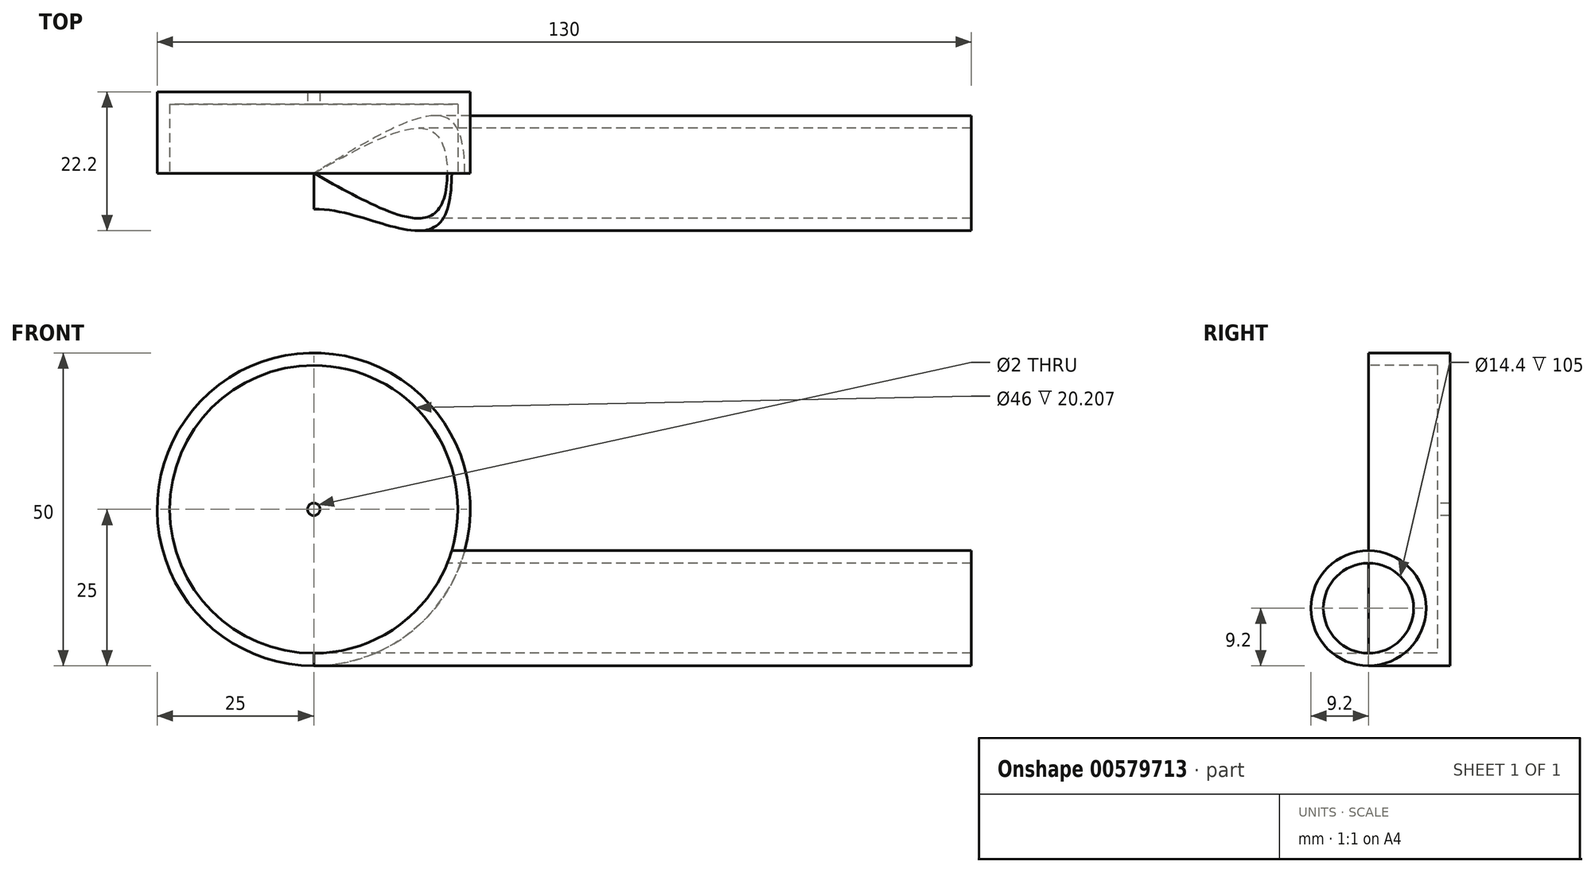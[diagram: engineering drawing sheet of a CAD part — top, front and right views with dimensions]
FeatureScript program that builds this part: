
annotation { "Feature Type Name" : "Feature", "Feature Type Description" : "" }
export const myFeature = defineFeature(function(context is Context, id is Id, definition is map)
    precondition{}
    {
        {
            var Q0;
            Q0=qCreatedBy(makeId("Front.planeOp"),FACE);
            var sketch = newSketch(context, id + "F0", { "sketchPlane" : qUnion([Q0])});
            skCircle(sketch, "E0", {"center": v(0, 0) * mm, "radius": 25 * mm});
            skCircle(sketch, "E1", {"center": v(0, 0) * mm, "radius": 1 * mm});
            skSolve(sketch);
        }
        {
            var Q0;
            Q0 = qSketchRegion(id + "F0", true);
            extrude(context, id + "F1", {"entities" : qUnion([Q0]), "depth" : 13 * mm, "offsetDistance" : 25.4 * mm});
        }
        {
            var Q0;
            Q0=makeQuery(id+"F1.opExtrude","CAP_FACE",FACE,{"disambiguationData":[OSD([sQuery(id+"F0.wireOp",EDGE,"E0"),sQuery(id+"F0.wireOp",EDGE,"E1")])],"isStart":true});
            var sketch = newSketch(context, id + "F2", { "sketchPlane" : qUnion([Q0])});
            skCircle(sketch, "E2", {"center": v(0, 0) * mm, "radius": 23 * mm});
            skSolve(sketch);
        }
        {
            var Q0;
            Q0 = qSketchRegion(id + "F2", true);
            extrude(context, id + "F3", {"entities" : qUnion([Q0]), "operationType" : NewBodyOperationType.REMOVE, "oppositeDirection" : true, "depth" : 11 * mm, "offsetDistance" : 25.4 * mm});
        }
        {
            var Q0;
            Q0=qCreatedBy(makeId("Right.planeOp"),FACE);
            var sketch = newSketch(context, id + "F4", { "sketchPlane" : qUnion([Q0])});
            skCircle(sketch, "E3", {"center": v(0, -15.8) * mm, "radius": 9.2 * mm});
            skCircle(sketch, "E4", {"center": v(0, -15.8) * mm, "radius": 7.2 * mm});
            skSolve(sketch);
        }
        {
            var Q0;
            Q0 = qSketchRegion(id + "F4", true);
            extrude(context, id + "F5", {"entities" : qUnion([Q0]), "operationType" : NewBodyOperationType.ADD, "oppositeDirection" : true, "depth" : 105 * mm, "offsetDistance" : 25.4 * mm});
        }
        {
            var Q0;
            Q0=makeQuery(id+"F4.imprint","IMPRINT",FACE,{"disambiguationData":[TD([[makeQuery(id+"F4.imprint","IMPRINT",EDGE,{"derivedFrom":sQuery(id+"F4.wireOp",EDGE,"E4")}),1.0]])]});
            extrude(context, id + "F6", {"entities" : qUnion([Q0]), "operationType" : NewBodyOperationType.REMOVE, "oppositeDirection" : true, "depth" : 50.8 * mm, "offsetDistance" : 25.4 * mm});
        }
        {
            var Q0;
            Q0=makeQuery(id+"F0.imprint","IMPRINT",FACE,{"disambiguationData":[TD([[makeQuery(id+"F0.imprint","IMPRINT",EDGE,{"derivedFrom":sQuery(id+"F0.wireOp",EDGE,"E1")}),1.0]])]});
            extrude(context, id + "F7", {"entities" : qUnion([Q0]), "operationType" : NewBodyOperationType.REMOVE, "oppositeDirection" : true, "depth" : 25.4 * mm, "offsetDistance" : 25.4 * mm});
        }
        {
            var Q0;
            Q0=makeQuery(id+"F3.boolean.opBoolean","COPY",FACE,{"derivedFrom":makeQuery(id+"F3.opExtrude","CAP_FACE",FACE,{"disambiguationData":[OSD([sQuery(id+"F2.wireOp",EDGE,"E2")])],"isStart":false})});
            var sketch = newSketch(context, id + "F8", { "sketchPlane" : qUnion([Q0])});
            skCircle(sketch, "E5", {"center": v(0, 0) * mm, "radius": 23 * mm});
            skSolve(sketch);
        }
        {
            var Q0;
            Q0 = qSketchRegion(id + "F8", true);
            extrude(context, id + "F9", {"entities" : qUnion([Q0]), "operationType" : NewBodyOperationType.REMOVE, "depth" : 25.4 * mm, "offsetDistance" : 25.4 * mm});
        }
        {
            var Q0;
            Q0=qCreatedBy(makeId("Front.planeOp"),FACE);
            var sketch = newSketch(context, id + "F10", { "sketchPlane" : qUnion([Q0])});
            skLineSegment(sketch, "E6", {"start": v(0, 74.01) * mm, "end": v(0, -66.07) * mm});
            skSolve(sketch);
        }
        {
            var Q0;
            Q0=makeQuery(id+"F1.opExtrude","SWEPT_BODY",BODY,{"disambiguationData":[OSD([sQuery(id+"F0.wireOp",EDGE,"E0"),sQuery(id+"F0.wireOp",EDGE,"E1")])]});
            var Q1;
            Q1=sQuery(id+"F10.wireOp",EDGE,"E6");
            transform(context, id + "F11", {"entities" : qUnion([Q0]), "transformType" : TransformType.ROTATION, "transformAxis" : qUnion([Q1]), "angle" : 180 * degree, "makeCopy" : false});
        }
    });
